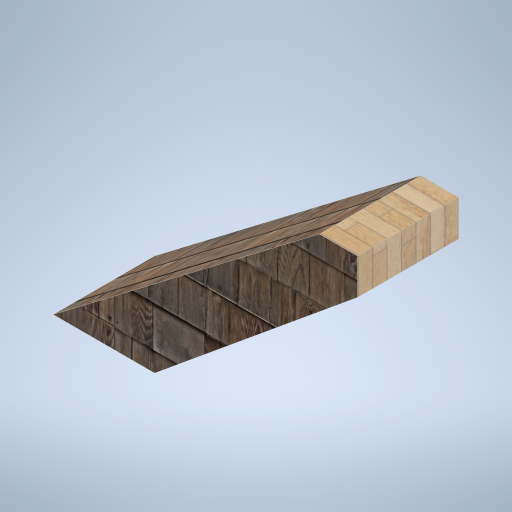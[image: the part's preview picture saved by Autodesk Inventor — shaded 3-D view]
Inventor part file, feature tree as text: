
AUTODESK INVENTOR PART (.ipt)
format: ipt  version: 2024.2 (Build 282272000, 272)  size: 329,728 bytes
history: native  units: mm
features: extrude x1, sketch x1
ambient origin geometry x8: Origin, YZ Plane, XZ Plane, XY Plane, X Axis, Y Axis, Z Axis, Center Point
bodies: Body1 (feature_tree)
feature tree (2):
  extrude  "Extrusion3"  Depth=400.0mm
  sketch  "Sketch1"  dims[d2=90.0deg d5=150.0mm d6=400.0mm d7=0.0mm]
